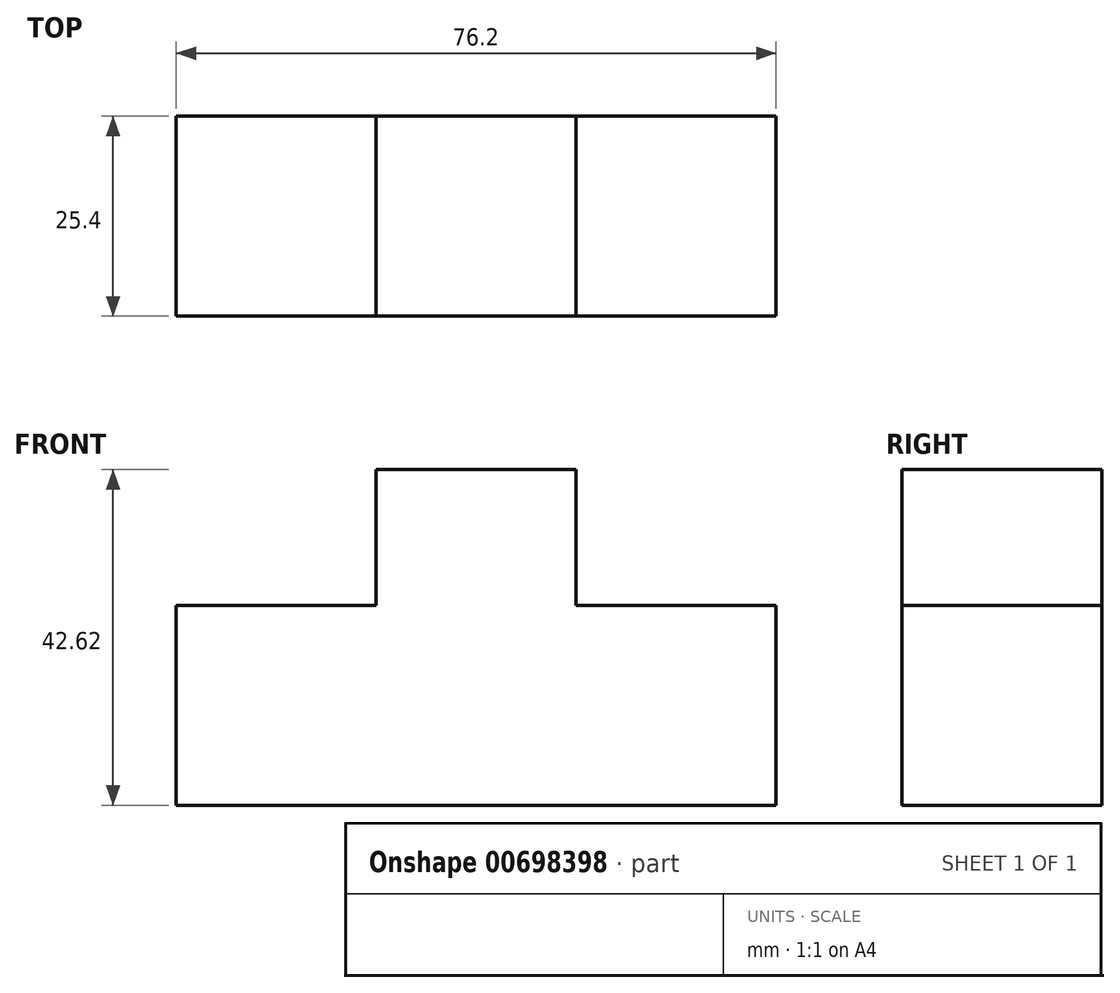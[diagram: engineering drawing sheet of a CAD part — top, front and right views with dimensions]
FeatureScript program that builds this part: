
annotation { "Feature Type Name" : "Feature", "Feature Type Description" : "" }
export const myFeature = defineFeature(function(context is Context, id is Id, definition is map)
    precondition{}
    {
        {
            var Q0;
            Q0=qCreatedBy(makeId("Front.planeOp"),FACE);
            var sketch = newSketch(context, id + "F0", { "sketchPlane" : qUnion([Q0])});
            skLineSegment(sketch, "E0.bottom", {"start": v(0, 0) * mm, "end": v(-25.4, 0) * mm});
            skLineSegment(sketch, "E0.top", {"start": v(0, 25.4) * mm, "end": v(-25.4, 25.4) * mm});
            skLineSegment(sketch, "E0.left", {"start": v(0, 0) * mm, "end": v(0, 25.4) * mm});
            skLineSegment(sketch, "E0.right", {"start": v(-25.4, 0) * mm, "end": v(-25.4, 25.4) * mm});
            skLineSegment(sketch, "E1.bottom", {"start": v(0, 25.4) * mm, "end": v(25.4, 25.4) * mm});
            skLineSegment(sketch, "E1.top", {"start": v(0, 0) * mm, "end": v(25.4, 0) * mm});
            skLineSegment(sketch, "E1.left", {"start": v(0, 25.4) * mm, "end": v(0, 0) * mm});
            skLineSegment(sketch, "E1.right", {"start": v(25.4, 25.4) * mm, "end": v(25.4, 0) * mm});
            skLineSegment(sketch, "E2.bottom", {"start": v(25.4, 25.4) * mm, "end": v(50.8, 25.4) * mm});
            skLineSegment(sketch, "E2.top", {"start": v(25.4, 0) * mm, "end": v(50.8, 0) * mm});
            skLineSegment(sketch, "E2.right", {"start": v(50.8, 25.4) * mm, "end": v(50.8, 0) * mm});
            skLineSegment(sketch, "E3.top", {"start": v(0, 42.62) * mm, "end": v(25.4, 42.62) * mm});
            skLineSegment(sketch, "E3.left", {"start": v(0, 25.4) * mm, "end": v(0, 42.62) * mm});
            skLineSegment(sketch, "E3.right", {"start": v(25.4, 25.4) * mm, "end": v(25.4, 42.62) * mm});
            skSolve(sketch);
        }
        {
            var Q0;
            Q0 = qSketchRegion(id + "F0", true);
            extrude(context, id + "F1", {"entities" : qUnion([Q0]), "depth" : 25.4 * mm, "offsetDistance" : 25.4 * mm});
        }
    });
